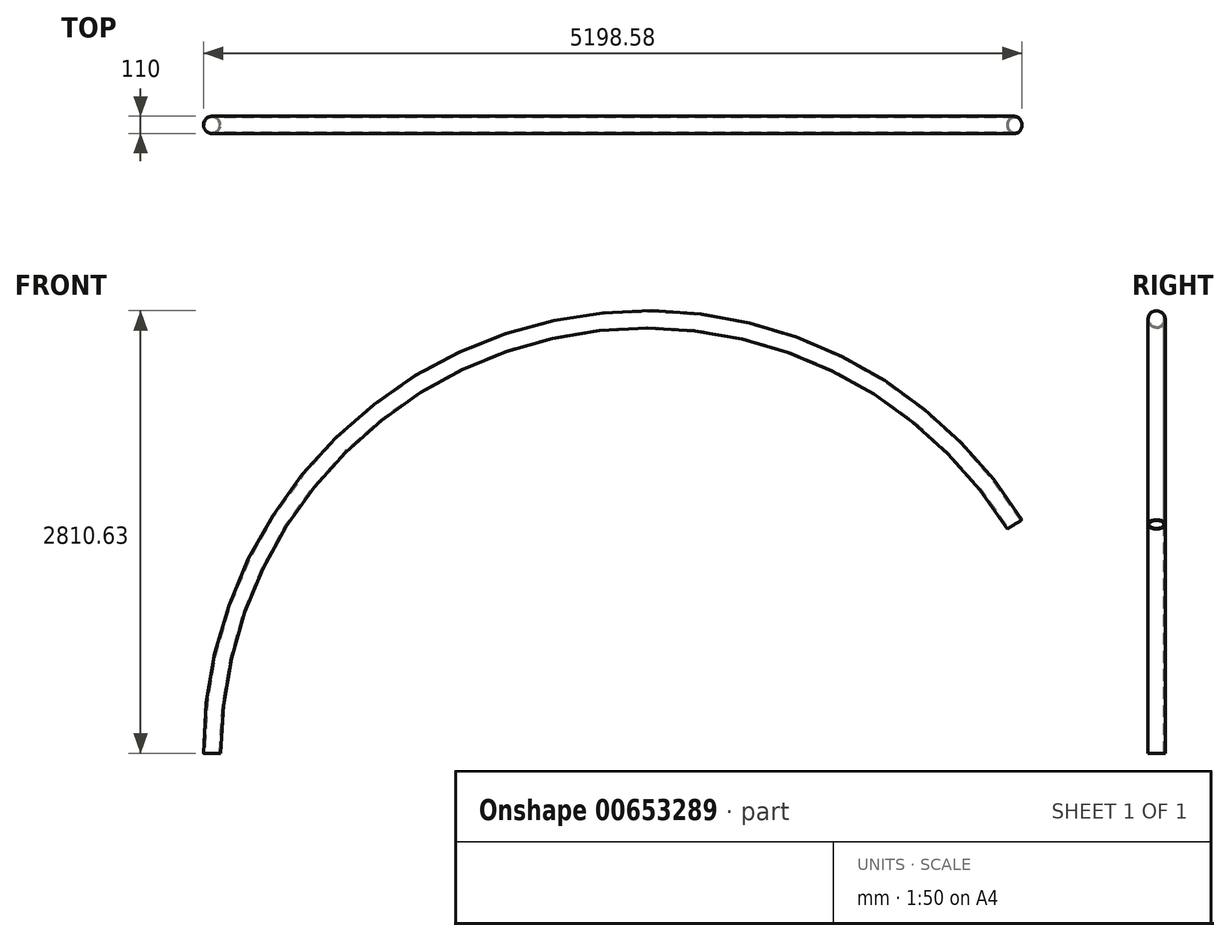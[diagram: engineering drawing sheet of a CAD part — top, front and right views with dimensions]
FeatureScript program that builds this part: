
annotation { "Feature Type Name" : "Feature", "Feature Type Description" : "" }
export const myFeature = defineFeature(function(context is Context, id is Id, definition is map)
    precondition{}
    {
        {
            var Q0;
            Q0=qCreatedBy(makeId("Top.planeOp"),FACE);
            var sketch = newSketch(context, id + "F0", { "sketchPlane" : qUnion([Q0])});
            skCircle(sketch, "E0", {"center": v(0, 0) * mm, "radius": 55 * mm});
            skCircle(sketch, "E1", {"center": v(0, 0) * mm, "radius": 48 * mm});
            skSolve(sketch);
        }
        {
            var Q0;
            Q0=qCreatedBy(makeId("Front.planeOp"),FACE);
            var sketch = newSketch(context, id + "F1", { "sketchPlane" : qUnion([Q0])});
            skPoint(sketch, "E2.0", {"position": v(0, 0) * mm});
            skArc(sketch, "E3", {"start": v(5096.85, 1453.32) * mm, "mid": v(2000, 2650) * mm, "end": v(0, 0) * mm});
            skSolve(sketch);
        }
        {
            var Q0;
            Q0=makeQuery(id+"F0.imprint","IMPRINT",FACE,{"disambiguationData":[TD([[makeQuery(id+"F0.imprint","IMPRINT",EDGE,{"derivedFrom":sQuery(id+"F0.wireOp",EDGE,"E0")}),1.0]])]});
            var Q1;
            Q1=sQuery(id+"F1.wireOp",EDGE,"E3");
            sweep(context, id + "F2", {"profiles" : qUnion([Q0]), "path" : qUnion([Q1])});
        }
    });
